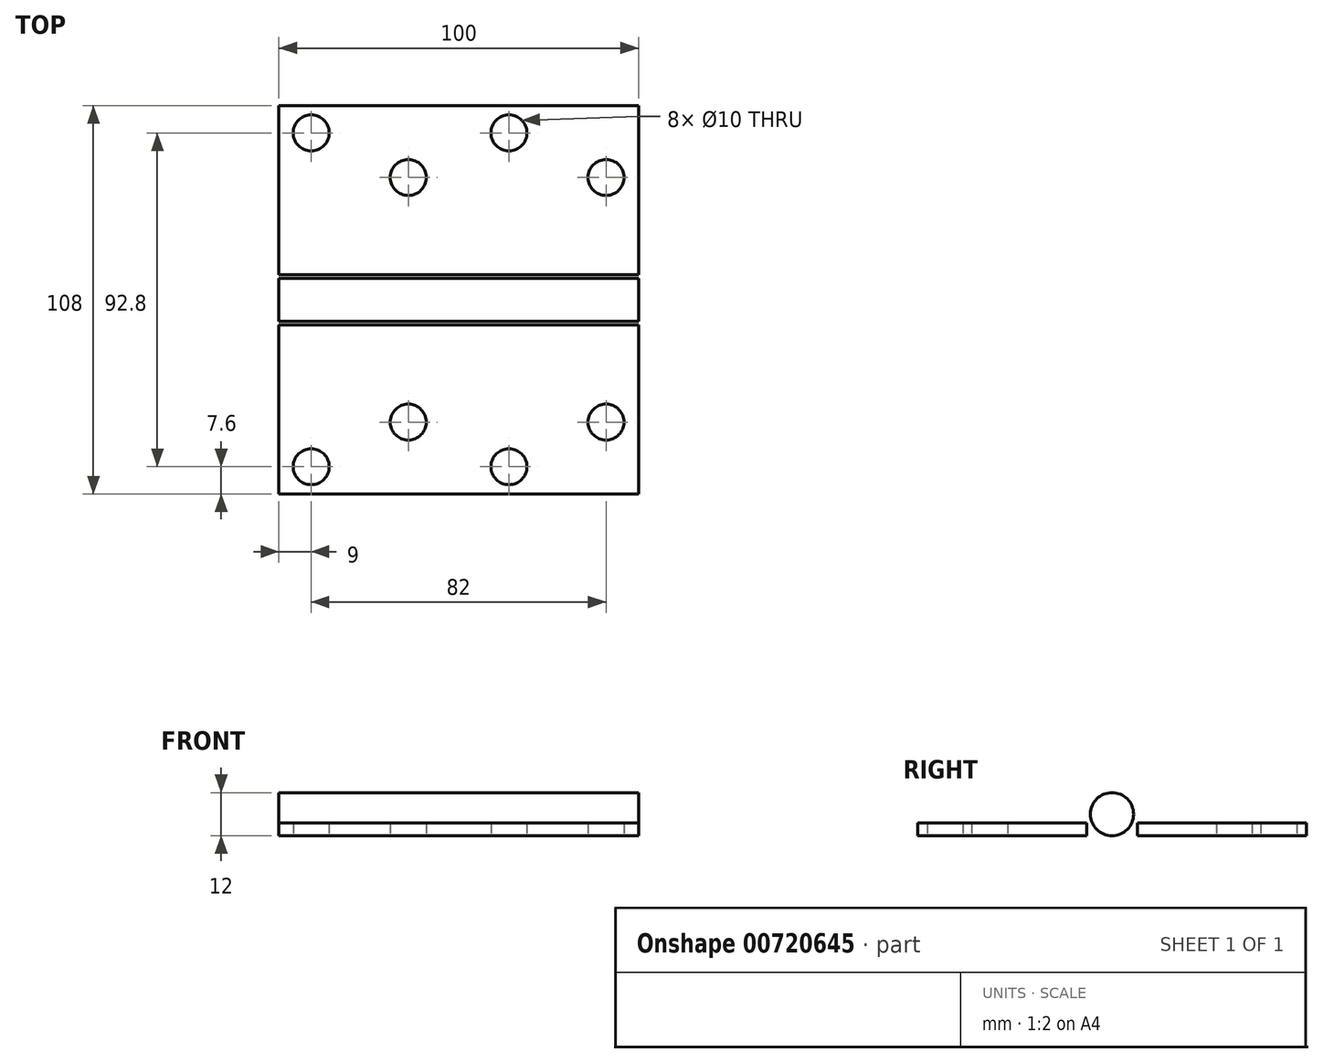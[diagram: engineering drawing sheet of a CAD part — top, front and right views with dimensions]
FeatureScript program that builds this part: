
annotation { "Feature Type Name" : "Feature", "Feature Type Description" : "" }
export const myFeature = defineFeature(function(context is Context, id is Id, definition is map)
    precondition{}
    {
        {
            var Q0;
            Q0=qCreatedBy(makeId("Top.planeOp"),FACE);
            var sketch = newSketch(context, id + "F0", { "sketchPlane" : qUnion([Q0])});
            skLineSegment(sketch, "E0.bottom", {"start": v(-50, 0) * mm, "end": v(50, 0) * mm});
            skLineSegment(sketch, "E0.top", {"start": v(-50, -47) * mm, "end": v(50, -47) * mm});
            skLineSegment(sketch, "E0.left", {"start": v(-50, 0) * mm, "end": v(-50, -47) * mm});
            skLineSegment(sketch, "E0.right", {"start": v(50, 0) * mm, "end": v(50, -47) * mm});
            skPoint(sketch, "E1", {"position": v(0, 0) * mm});
            skCircle(sketch, "E2", {"center": v(-41, -39.4) * mm, "radius": 5 * mm});
            skCircle(sketch, "E3", {"center": v(-14, -27) * mm, "radius": 5 * mm});
            skCircle(sketch, "E4", {"center": v(41, -27) * mm, "radius": 5 * mm});
            skCircle(sketch, "E5", {"center": v(14, -39.4) * mm, "radius": 5 * mm});
            skLineSegment(sketch, "E6", {"start": v(-41, -39.4) * mm, "end": v(59.2, -39.4) * mm, "construction": true});
            skLineSegment(sketch, "E7", {"start": v(-14, -27) * mm, "end": v(55.15, -27) * mm, "construction": true});
            skLineSegment(sketch, "E8", {"start": v(-69.43, 7) * mm, "end": v(82.98, 7) * mm, "construction": true});
            skLineSegment(sketch, "E9.MirrorCS", {"start": v(-50, 14) * mm, "end": v(-50, 61) * mm});
            skCircle(sketch, "E10.MirrorC", {"center": v(41, 41) * mm, "radius": 5 * mm});
            skCircle(sketch, "E11.MirrorC", {"center": v(14, 53.4) * mm, "radius": 5 * mm});
            skCircle(sketch, "E12.MirrorC", {"center": v(-14, 41) * mm, "radius": 5 * mm});
            skLineSegment(sketch, "E13.MirrorCS", {"start": v(-50, 61) * mm, "end": v(50, 61) * mm});
            skLineSegment(sketch, "E14.MirrorCS", {"start": v(-50, 14) * mm, "end": v(50, 14) * mm});
            skCircle(sketch, "E15.MirrorC", {"center": v(-41, 53.4) * mm, "radius": 5 * mm});
            skLineSegment(sketch, "E16.MirrorCS", {"start": v(50, 14) * mm, "end": v(50, 61) * mm});
            skPoint(sketch, "E17.MirrorP", {"position": v(0, 14) * mm});
            skLineSegment(sketch, "E18.MirrorCS", {"start": v(-41, 53.4) * mm, "end": v(59.2, 53.4) * mm, "construction": true});
            skLineSegment(sketch, "E19.MirrorCS", {"start": v(-14, 41) * mm, "end": v(55.15, 41) * mm, "construction": true});
            skSolve(sketch);
        }
        {
            var Q0;
            Q0 = qSketchRegion(id + "F0", true);
            extrude(context, id + "F1", {"entities" : qUnion([Q0]), "depth" : 3.6 * mm, "offsetDistance" : 25 * mm});
        }
        {
            var Q0;
            Q0=qCreatedBy(makeId("Right.planeOp"),FACE);
            var sketch = newSketch(context, id + "F2", { "sketchPlane" : qUnion([Q0])});
            skCircle(sketch, "E20", {"center": v(7, 6) * mm, "radius": 6 * mm});
            skLineSegment(sketch, "E21", {"start": v(0, 0) * mm, "end": v(0, 27.56) * mm, "construction": true});
            skLineSegment(sketch, "E22", {"start": v(0, 0) * mm, "end": v(22.03, 0) * mm, "construction": true});
            skSolve(sketch);
        }
        {
            var Q0;
            Q0 = qSketchRegion(id + "F2", true);
            extrude(context, id + "F3", {"entities" : qUnion([Q0]), "depth" : 50 * mm, "offsetDistance" : 25 * mm, "hasSecondDirection" : true, "secondDirectionOppositeDirection" : true, "secondDirectionDepth" : 50 * mm});
        }
    });
